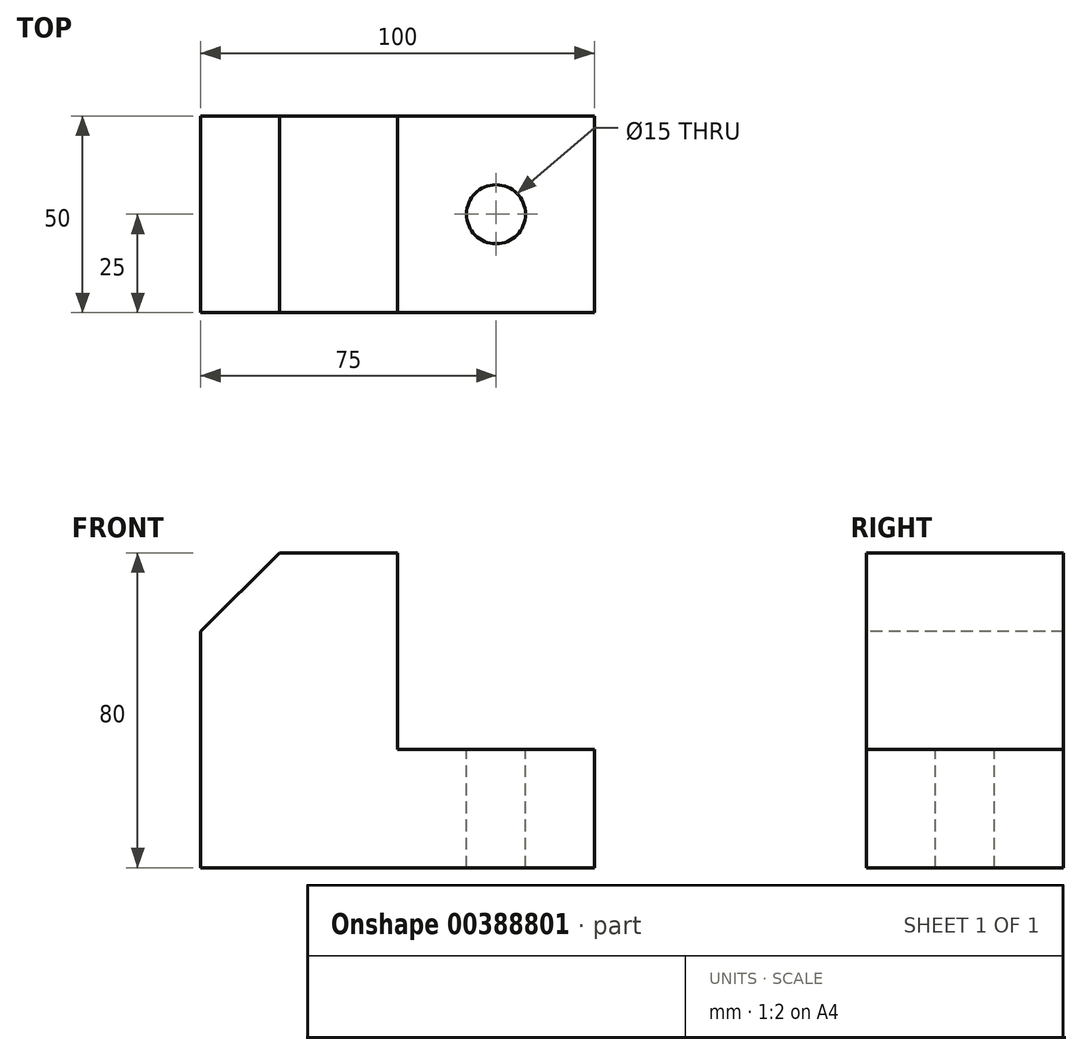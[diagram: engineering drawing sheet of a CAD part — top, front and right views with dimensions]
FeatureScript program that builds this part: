
annotation { "Feature Type Name" : "Feature", "Feature Type Description" : "" }
export const myFeature = defineFeature(function(context is Context, id is Id, definition is map)
    precondition{}
    {
        {
            var Q0;
            Q0=qCreatedBy(makeId("Top.planeOp"),FACE);
            var sketch = newSketch(context, id + "F0", { "sketchPlane" : qUnion([Q0])});
            skLineSegment(sketch, "E0.bottom", {"start": v(0, 0) * mm, "end": v(100, 0) * mm});
            skLineSegment(sketch, "E0.top", {"start": v(0, 50) * mm, "end": v(100, 50) * mm});
            skLineSegment(sketch, "E0.left", {"start": v(0, 0) * mm, "end": v(0, 50) * mm});
            skLineSegment(sketch, "E0.right", {"start": v(100, 0) * mm, "end": v(100, 50) * mm});
            skSolve(sketch);
        }
        {
            var Q0;
            Q0 = qSketchRegion(id + "F0", true);
            extrude(context, id + "F1", {"entities" : qUnion([Q0]), "depth" : 80 * mm});
        }
        {
            var Q0;
            Q0=makeQuery(id+"F1.opExtrude","SWEPT_FACE",FACE,{"disambiguationData":[OSD([sQuery(id+"F0.wireOp",EDGE,"E0.bottom")])]});
            var sketch = newSketch(context, id + "F2", { "sketchPlane" : qUnion([Q0])});
            skLineSegment(sketch, "E1.bottom", {"start": v(100, 80) * mm, "end": v(50, 80) * mm});
            skLineSegment(sketch, "E1.top", {"start": v(100, 30) * mm, "end": v(50, 30) * mm});
            skLineSegment(sketch, "E1.left", {"start": v(100, 80) * mm, "end": v(100, 30) * mm});
            skLineSegment(sketch, "E1.right", {"start": v(50, 80) * mm, "end": v(50, 30) * mm});
            skSolve(sketch);
        }
        {
            var Q0;
            Q0 = qSketchRegion(id + "F2", true);
            extrude(context, id + "F3", {"entities" : qUnion([Q0]), "operationType" : NewBodyOperationType.REMOVE, "endBound" : BoundingType.UP_TO_NEXT, "oppositeDirection" : true, "depth" : 22 * mm});
        }
        {
            var Q0;
            Q0=makeQuery(id+"F1.opExtrude","SWEPT_FACE",FACE,{"disambiguationData":[OSD([sQuery(id+"F0.wireOp",EDGE,"E0.bottom")])]});
            var sketch = newSketch(context, id + "F4", { "sketchPlane" : qUnion([Q0])});
            skLineSegment(sketch, "E2", {"start": v(0, 80) * mm, "end": v(20, 80) * mm});
            skLineSegment(sketch, "E3", {"start": v(20, 80) * mm, "end": v(0, 60) * mm});
            skLineSegment(sketch, "E4", {"start": v(0, 60) * mm, "end": v(0, 80) * mm});
            skSolve(sketch);
        }
        {
            var Q0;
            Q0 = qSketchRegion(id + "F4", true);
            extrude(context, id + "F5", {"entities" : qUnion([Q0]), "operationType" : NewBodyOperationType.REMOVE, "endBound" : BoundingType.UP_TO_NEXT, "oppositeDirection" : true, "depth" : 22 * mm});
        }
        {
            var Q0;
            Q0=makeQuery(id+"F3.boolean.opBoolean","COPY",FACE,{"derivedFrom":makeQuery(id+"F3.opExtrude","SWEPT_FACE",FACE,{"disambiguationData":[OSD([sQuery(id+"F2.wireOp",EDGE,"E1.top")])]})});
            var sketch = newSketch(context, id + "F6", { "sketchPlane" : qUnion([Q0])});
            skPoint(sketch, "E5.centerSnap0", {"position": v(50, 25) * mm});
            skCircle(sketch, "E6", {"center": v(75, 25) * mm, "radius": 7.5 * mm});
            skSolve(sketch);
        }
        {
            var Q0;
            Q0 = qSketchRegion(id + "F6", true);
            extrude(context, id + "F7", {"entities" : qUnion([Q0]), "operationType" : NewBodyOperationType.REMOVE, "endBound" : BoundingType.UP_TO_NEXT, "oppositeDirection" : true, "depth" : 25 * mm});
        }
    });
